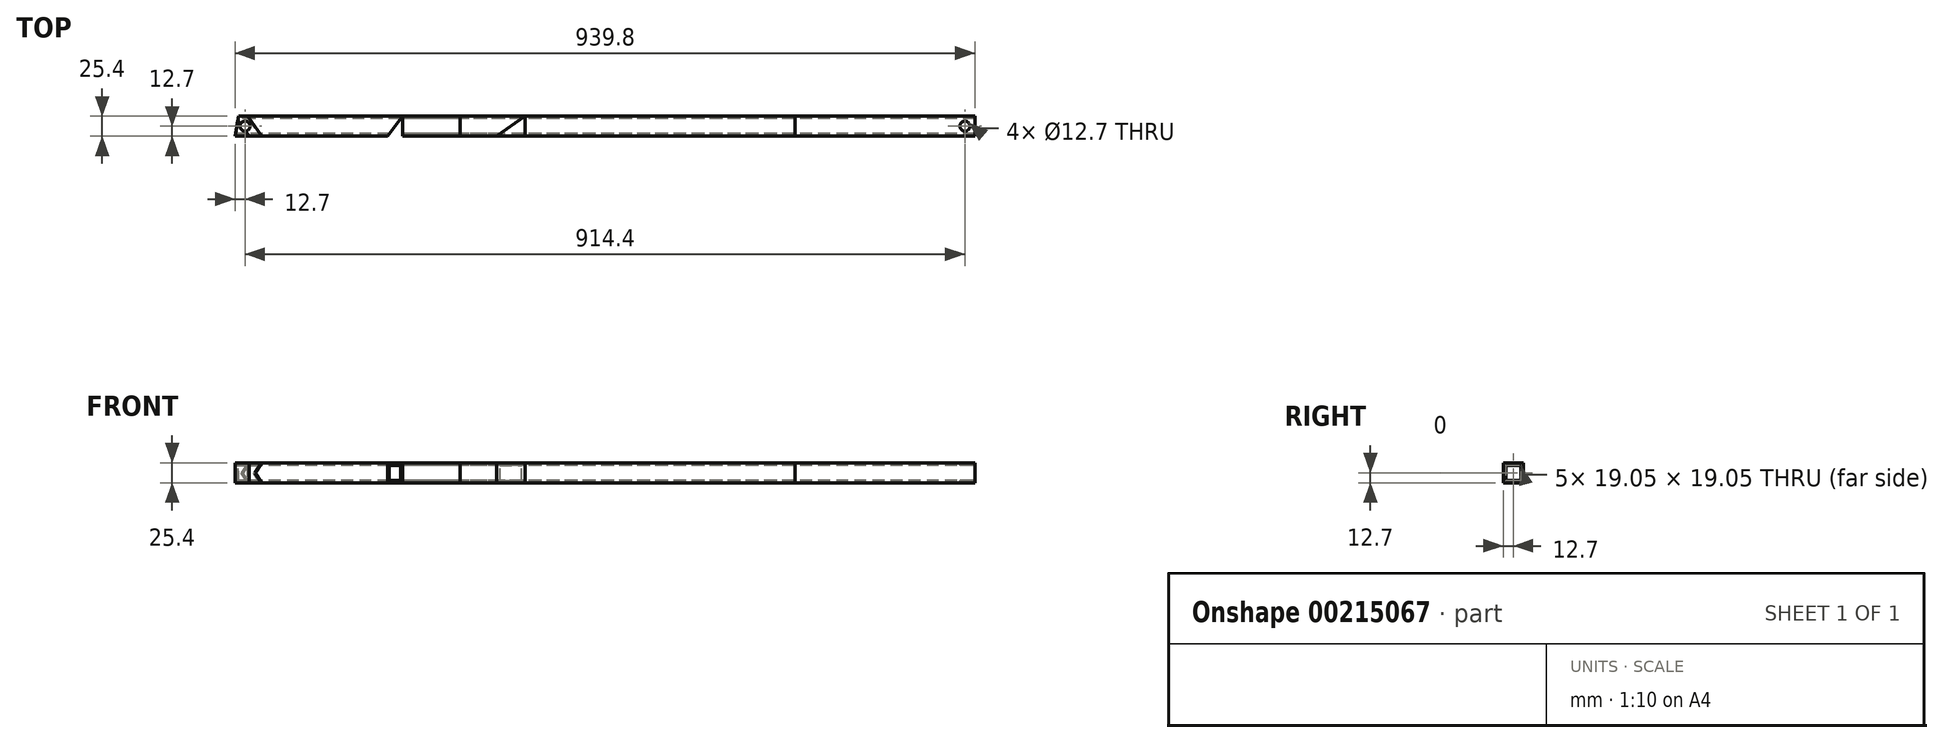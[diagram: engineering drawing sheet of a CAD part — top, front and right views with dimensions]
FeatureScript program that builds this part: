
annotation { "Feature Type Name" : "Feature", "Feature Type Description" : "" }
export const myFeature = defineFeature(function(context is Context, id is Id, definition is map)
    precondition{}
    {
        {
            var Q0;
            Q0=qCreatedBy(makeId("Right.planeOp"),FACE);
            var sketch = newSketch(context, id + "F0", { "sketchPlane" : qUnion([Q0])});
            skLineSegment(sketch, "E0.bottom", {"start": v(0, 0) * mm, "end": v(25.4, 0) * mm});
            skLineSegment(sketch, "E0.top", {"start": v(0, 25.4) * mm, "end": v(25.4, 25.4) * mm});
            skLineSegment(sketch, "E0.left", {"start": v(0, 0) * mm, "end": v(0, 25.4) * mm});
            skLineSegment(sketch, "E0.right", {"start": v(25.4, 0) * mm, "end": v(25.4, 25.4) * mm});
            skLineSegment(sketch, "E1.bottom", {"start": v(3.17, 3.18) * mm, "end": v(22.22, 3.18) * mm});
            skLineSegment(sketch, "E1.top", {"start": v(3.17, 22.22) * mm, "end": v(22.22, 22.22) * mm});
            skLineSegment(sketch, "E1.left", {"start": v(3.17, 3.18) * mm, "end": v(3.17, 22.22) * mm});
            skLineSegment(sketch, "E1.right", {"start": v(22.22, 3.18) * mm, "end": v(22.22, 22.22) * mm});
            skSolve(sketch);
        }
        {
            var Q0;
            Q0 = qSketchRegion(id + "F0", true);
            extrude(context, id + "F1", {"entities" : qUnion([Q0]), "depth" : 939.8 * mm, "offsetDistance" : 25.4 * mm});
        }
        {
            var Q0;
            Q0=qCreatedBy(makeId("Right.planeOp"),FACE);
            var sketch = newSketch(context, id + "F2", { "sketchPlane" : qUnion([Q0])});
            skLineSegment(sketch, "E2.bottom", {"start": v(0, 0) * mm, "end": v(25.4, 0) * mm});
            skLineSegment(sketch, "E2.top", {"start": v(0, 25.4) * mm, "end": v(25.4, 25.4) * mm});
            skLineSegment(sketch, "E2.left", {"start": v(0, 0) * mm, "end": v(0, 25.4) * mm});
            skLineSegment(sketch, "E2.right", {"start": v(25.4, 0) * mm, "end": v(25.4, 25.4) * mm});
            skLineSegment(sketch, "E3.bottom", {"start": v(3.17, 3.18) * mm, "end": v(22.23, 3.18) * mm});
            skLineSegment(sketch, "E3.top", {"start": v(3.17, 22.22) * mm, "end": v(22.22, 22.22) * mm});
            skLineSegment(sketch, "E3.left", {"start": v(3.17, 3.18) * mm, "end": v(3.17, 22.22) * mm});
            skLineSegment(sketch, "E3.right", {"start": v(22.23, 3.18) * mm, "end": v(22.22, 22.22) * mm});
            skSolve(sketch);
        }
        {
            var Q0;
            Q0 = qSketchRegion(id + "F2", true);
            extrude(context, id + "F3", {"entities" : qUnion([Q0]), "depth" : 368.3 * mm, "offsetDistance" : 25.4 * mm});
        }
        {
            var Q0;
            Q0=makeQuery(id+"F3.opExtrude","SWEPT_FACE",FACE,{"disambiguationData":[OSD([sQuery(id+"F2.wireOp",EDGE,"E2.top")])]});
            var sketch = newSketch(context, id + "F4", { "sketchPlane" : qUnion([Q0])});
            skLineSegment(sketch, "E4", {"start": v(0, 25.4) * mm, "end": v(0, 0) * mm});
            skLineSegment(sketch, "E5", {"start": v(0, 0) * mm, "end": v(17.79, 0) * mm});
            skLineSegment(sketch, "E6", {"start": v(17.79, 0) * mm, "end": v(0, 25.4) * mm});
            skLineSegment(sketch, "E7", {"start": v(368.3, 25.4) * mm, "end": v(368.3, 0) * mm});
            skLineSegment(sketch, "E8", {"start": v(368.3, 0) * mm, "end": v(332.03, 0) * mm});
            skLineSegment(sketch, "E9", {"start": v(332.03, 0) * mm, "end": v(368.3, 25.4) * mm});
            skSolve(sketch);
        }
        {
            var Q0;
            Q0 = qSketchRegion(id + "F4", true);
            var Q1;
            Q1=makeQuery(id+"F3.opExtrude","SWEPT_FACE",FACE,{"disambiguationData":[OSD([sQuery(id+"F2.wireOp",EDGE,"E2.bottom")])]});
            extrude(context, id + "F5", {"entities" : qUnion([Q0]), "operationType" : NewBodyOperationType.REMOVE, "endBound" : BoundingType.UP_TO_SURFACE, "oppositeDirection" : true, "depth" : 25.4 * mm, "endBoundEntityFace" : qUnion([Q1]), "offsetDistance" : 25.4 * mm});
        }
        {
            var Q0;
            Q0=qCreatedBy(makeId("Right.planeOp"),FACE);
            var sketch = newSketch(context, id + "F6", { "sketchPlane" : qUnion([Q0])});
            skLineSegment(sketch, "E10.bottom", {"start": v(0, 0) * mm, "end": v(25.4, 0) * mm});
            skLineSegment(sketch, "E10.top", {"start": v(0, 25.4) * mm, "end": v(25.4, 25.4) * mm});
            skLineSegment(sketch, "E10.left", {"start": v(0, 0) * mm, "end": v(0, 25.4) * mm});
            skLineSegment(sketch, "E10.right", {"start": v(25.4, 0) * mm, "end": v(25.4, 25.4) * mm});
            skLineSegment(sketch, "E11.bottom", {"start": v(3.17, 3.18) * mm, "end": v(22.22, 3.18) * mm});
            skLineSegment(sketch, "E11.top", {"start": v(3.17, 22.22) * mm, "end": v(22.22, 22.22) * mm});
            skLineSegment(sketch, "E11.left", {"start": v(3.17, 3.18) * mm, "end": v(3.17, 22.22) * mm});
            skLineSegment(sketch, "E11.right", {"start": v(22.22, 3.18) * mm, "end": v(22.22, 22.22) * mm});
            skSolve(sketch);
        }
        {
            var Q0;
            Q0 = qSketchRegion(id + "F6", true);
            extrude(context, id + "F7", {"entities" : qUnion([Q0]), "depth" : 285.75 * mm, "offsetDistance" : 25.4 * mm});
        }
        {
            var Q0;
            Q0=qCreatedBy(makeId("Right.planeOp"),FACE);
            var sketch = newSketch(context, id + "F8", { "sketchPlane" : qUnion([Q0])});
            skLineSegment(sketch, "E12.bottom", {"start": v(0, 0) * mm, "end": v(25.4, 0) * mm});
            skLineSegment(sketch, "E12.top", {"start": v(0, 25.4) * mm, "end": v(25.4, 25.4) * mm});
            skLineSegment(sketch, "E12.left", {"start": v(0, 0) * mm, "end": v(0, 25.4) * mm});
            skLineSegment(sketch, "E12.right", {"start": v(25.4, 0) * mm, "end": v(25.4, 25.4) * mm});
            skLineSegment(sketch, "E13.bottom", {"start": v(3.17, 3.18) * mm, "end": v(22.23, 3.18) * mm});
            skLineSegment(sketch, "E13.top", {"start": v(3.17, 22.22) * mm, "end": v(22.22, 22.22) * mm});
            skLineSegment(sketch, "E13.left", {"start": v(3.17, 3.18) * mm, "end": v(3.17, 22.22) * mm});
            skLineSegment(sketch, "E13.right", {"start": v(22.23, 3.18) * mm, "end": v(22.22, 22.22) * mm});
            skSolve(sketch);
        }
        {
            var Q0;
            Q0 = qSketchRegion(id + "F8", true);
            extrude(context, id + "F9", {"entities" : qUnion([Q0]), "depth" : 711.2 * mm, "offsetDistance" : 25.4 * mm});
        }
        {
            var Q0;
            Q0=makeQuery(id+"F3.opExtrude","SWEPT_BODY",BODY,{"disambiguationData":[OSD([sQuery(id+"F2.wireOp",EDGE,"E2.bottom"),sQuery(id+"F2.wireOp",EDGE,"E2.top"),sQuery(id+"F2.wireOp",EDGE,"E2.left"),sQuery(id+"F2.wireOp",EDGE,"E2.right"),sQuery(id+"F2.wireOp",EDGE,"E3.bottom"),sQuery(id+"F2.wireOp",EDGE,"E3.top"),sQuery(id+"F2.wireOp",EDGE,"E3.left"),sQuery(id+"F2.wireOp",EDGE,"E3.right")])]});
            transform(context, id + "F10", {"entities" : qUnion([Q0]), "transformType" : TransformType.COPY});
        }
        {
            var Q0;
            {var subQ0=sQuery(id+"F2.wireOp",EDGE,"E2.right");Q0=makeQuery(id+"F10.opPattern","COPY",EDGE,{"derivedFrom":makeQuery(id+"F5.boolean.opBoolean","MERGE",EDGE,{"derivedFrom":[makeQuery(id+"F3.opExtrude","CAP_EDGE",EDGE,{"disambiguationData":[OSD([subQ0])],"isStart":true}),makeQuery(id+"F5.opExtrude","SWEPT_EDGE",EDGE,{"disambiguationData":[OSD([sQuery(id+"F2.wireOp",EDGE,"E2.top"),subQ0,sQuery(id+"F4.wireOp",EDGE,"E4"),sQuery(id+"F4.wireOp",EDGE,"E6")])]})]}),"instanceName":"1"});}
            cPlane(context, id + "F11", {"entities" : qUnion([Q0]), "cplaneType" : CPlaneType.LINE_ANGLE, "offset" : 25.4 * mm, "angle" : 55 * degree, "oppositeDirection" : true, "width" : 152.4 * mm, "height" : 152.4 * mm});
        }
        {
            var Q0;
            Q0=qCreatedBy(id+"F11.planeOp",FACE);
            var sketch = newSketch(context, id + "F12", { "sketchPlane" : qUnion([Q0])});
            skLineSegment(sketch, "E14.0", {"start": v(14.57, 0) * mm, "end": v(14.57, 25.4) * mm});
            skLineSegment(sketch, "E15.0", {"start": v(316.26, 25.4) * mm, "end": v(14.57, 25.4) * mm});
            skLineSegment(sketch, "E16.0", {"start": v(316.26, 0) * mm, "end": v(14.57, 0) * mm});
            skLineSegment(sketch, "E17", {"start": v(14.57, 25.4) * mm, "end": v(27.51, 0) * mm});
            skLineSegment(sketch, "E18", {"start": v(27.51, 0) * mm, "end": v(14.57, 0) * mm});
            skSolve(sketch);
        }
        {
            var Q0;
            {var subQ0=sQuery(id+"F12.wireOp",EDGE,"E14.0");Q0=makeQuery(id+"F12.imprint","IMPRINT",FACE,{"disambiguationData":[TD([[makeQuery(id+"F12.imprint","IMPRINT",EDGE,{"derivedFrom":subQ0}),-1.0]])]});}
            var Q1;
            Q1=makeQuery(id+"F10.opPattern","COPY",FACE,{"derivedFrom":makeQuery(id+"F3.opExtrude","SWEPT_FACE",FACE,{"disambiguationData":[OSD([sQuery(id+"F2.wireOp",EDGE,"E2.left")])]}),"instanceName":"1"});
            extrude(context, id + "F13", {"entities" : qUnion([Q0]), "operationType" : NewBodyOperationType.REMOVE, "endBound" : BoundingType.UP_TO_SURFACE, "depth" : 25.4 * mm, "endBoundEntityFace" : qUnion([Q1]), "offsetDistance" : 25.4 * mm});
        }
        {
            var Q0;
            Q0=makeQuery(id+"F3.opExtrude","SWEPT_BODY",BODY,{"disambiguationData":[OSD([sQuery(id+"F2.wireOp",EDGE,"E2.bottom"),sQuery(id+"F2.wireOp",EDGE,"E2.top"),sQuery(id+"F2.wireOp",EDGE,"E2.left"),sQuery(id+"F2.wireOp",EDGE,"E2.right"),sQuery(id+"F2.wireOp",EDGE,"E3.bottom"),sQuery(id+"F2.wireOp",EDGE,"E3.top"),sQuery(id+"F2.wireOp",EDGE,"E3.left"),sQuery(id+"F2.wireOp",EDGE,"E3.right")])]});
            transform(context, id + "F14", {"entities" : qUnion([Q0]), "transformType" : TransformType.COPY});
        }
        {
            var Q0;
            Q0=qCreatedBy(id+"F11.planeOp",FACE);
            var sketch = newSketch(context, id + "F15", { "sketchPlane" : qUnion([Q0])});
            skLineSegment(sketch, "E19.0", {"start": v(14.57, 0) * mm, "end": v(14.57, 25.4) * mm});
            skLineSegment(sketch, "E20.0", {"start": v(316.26, 0) * mm, "end": v(14.57, 0) * mm});
            skLineSegment(sketch, "E21.0", {"start": v(316.26, 25.4) * mm, "end": v(14.57, 25.4) * mm});
            skLineSegment(sketch, "E22", {"start": v(14.57, 0) * mm, "end": v(27.51, 25.4) * mm});
            skLineSegment(sketch, "E23", {"start": v(27.51, 25.4) * mm, "end": v(14.57, 25.4) * mm});
            skSolve(sketch);
        }
        {
            var Q0;
            {var subQ0=sQuery(id+"F15.wireOp",EDGE,"E19.0");Q0=makeQuery(id+"F15.imprint","IMPRINT",FACE,{"disambiguationData":[TD([[makeQuery(id+"F15.imprint","IMPRINT",EDGE,{"derivedFrom":subQ0}),-1.0]])]});}
            var Q1;
            Q1=makeQuery(id+"F14.opPattern","COPY",FACE,{"derivedFrom":makeQuery(id+"F3.opExtrude","SWEPT_FACE",FACE,{"disambiguationData":[OSD([sQuery(id+"F2.wireOp",EDGE,"E2.left")])]}),"instanceName":"1"});
            extrude(context, id + "F16", {"entities" : qUnion([Q0]), "operationType" : NewBodyOperationType.REMOVE, "endBound" : BoundingType.UP_TO_SURFACE, "depth" : 25.4 * mm, "endBoundEntityFace" : qUnion([Q1]), "offsetDistance" : 25.4 * mm});
        }
        {
            var Q0;
            Q0=qCreatedBy(makeId("Right.planeOp"),FACE);
            var sketch = newSketch(context, id + "F17", { "sketchPlane" : qUnion([Q0])});
            skLineSegment(sketch, "E24.bottom", {"start": v(0, 0) * mm, "end": v(25.4, 0) * mm});
            skLineSegment(sketch, "E24.top", {"start": v(0, 25.4) * mm, "end": v(25.4, 25.4) * mm});
            skLineSegment(sketch, "E24.left", {"start": v(0, 0) * mm, "end": v(0, 25.4) * mm});
            skLineSegment(sketch, "E24.right", {"start": v(25.4, 0) * mm, "end": v(25.4, 25.4) * mm});
            skLineSegment(sketch, "E25.bottom", {"start": v(3.18, 3.18) * mm, "end": v(22.22, 3.18) * mm});
            skLineSegment(sketch, "E25.top", {"start": v(3.17, 22.22) * mm, "end": v(22.22, 22.22) * mm});
            skLineSegment(sketch, "E25.left", {"start": v(3.17, 3.18) * mm, "end": v(3.17, 22.22) * mm});
            skLineSegment(sketch, "E25.right", {"start": v(22.22, 3.18) * mm, "end": v(22.22, 22.22) * mm});
            skSolve(sketch);
        }
        {
            var Q0;
            Q0 = qSketchRegion(id + "F17", true);
            extrude(context, id + "F18", {"entities" : qUnion([Q0]), "depth" : 212.72 * mm, "offsetDistance" : 25.4 * mm});
        }
        {
            var Q0;
            Q0=makeQuery(id+"F18.opExtrude","SWEPT_FACE",FACE,{"disambiguationData":[OSD([sQuery(id+"F17.wireOp",EDGE,"E24.top")])]});
            var sketch = newSketch(context, id + "F19", { "sketchPlane" : qUnion([Q0])});
            skLineSegment(sketch, "E26", {"start": v(0, 0) * mm, "end": v(4.48, 25.4) * mm});
            skLineSegment(sketch, "E27", {"start": v(4.48, 25.4) * mm, "end": v(0, 25.4) * mm});
            skLineSegment(sketch, "E28", {"start": v(0, 25.4) * mm, "end": v(0, 0) * mm});
            skLineSegment(sketch, "E29", {"start": v(212.73, 25.4) * mm, "end": v(193.58, 0) * mm});
            skLineSegment(sketch, "E30", {"start": v(193.58, 0) * mm, "end": v(212.73, 0) * mm});
            skLineSegment(sketch, "E31", {"start": v(212.73, 0) * mm, "end": v(212.73, 25.4) * mm});
            skSolve(sketch);
        }
        {
            var Q0;
            Q0=makeQuery(id+"F19.imprint","IMPRINT",FACE,{"disambiguationData":[TD([[makeQuery(id+"F19.imprint","IMPRINT",EDGE,{"derivedFrom":sQuery(id+"F19.wireOp",EDGE,"E29")}),1.0]])]});
            var Q1;
            Q1=makeQuery(id+"F19.imprint","IMPRINT",FACE,{"disambiguationData":[TD([[makeQuery(id+"F19.imprint","IMPRINT",EDGE,{"derivedFrom":sQuery(id+"F19.wireOp",EDGE,"E26")}),1.0]])]});
            var Q2;
            Q2=makeQuery(id+"F18.opExtrude","SWEPT_FACE",FACE,{"disambiguationData":[OSD([sQuery(id+"F17.wireOp",EDGE,"E24.bottom")])]});
            extrude(context, id + "F20", {"entities" : qUnion([Q0, Q1]), "operationType" : NewBodyOperationType.REMOVE, "endBound" : BoundingType.UP_TO_SURFACE, "oppositeDirection" : true, "depth" : 25.4 * mm, "endBoundEntityFace" : qUnion([Q2]), "offsetDistance" : 25.4 * mm});
        }
        {
            var Q0;
            Q0=makeQuery(id+"F1.opExtrude","SWEPT_FACE",FACE,{"disambiguationData":[OSD([sQuery(id+"F0.wireOp",EDGE,"E0.top")])]});
            var sketch = newSketch(context, id + "F21", { "sketchPlane" : qUnion([Q0])});
            skCircle(sketch, "E32", {"center": v(12.7, 12.7) * mm, "radius": 6.35 * mm});
            skCircle(sketch, "E33", {"center": v(927.1, 12.7) * mm, "radius": 6.35 * mm});
            skPoint(sketch, "E34", {"position": v(-20.38, 12.7) * mm});
            skSolve(sketch);
        }
        {
            var Q0;
            Q0 = qSketchRegion(id + "F21", true);
            var Q1;
            Q1=makeQuery(id+"F1.opExtrude","SWEPT_FACE",FACE,{"disambiguationData":[OSD([sQuery(id+"F0.wireOp",EDGE,"E0.bottom")])]});
            extrude(context, id + "F22", {"entities" : qUnion([Q0]), "operationType" : NewBodyOperationType.REMOVE, "endBound" : BoundingType.UP_TO_SURFACE, "oppositeDirection" : true, "depth" : 25.4 * mm, "endBoundEntityFace" : qUnion([Q1]), "offsetDistance" : 25.4 * mm});
        }
    });
